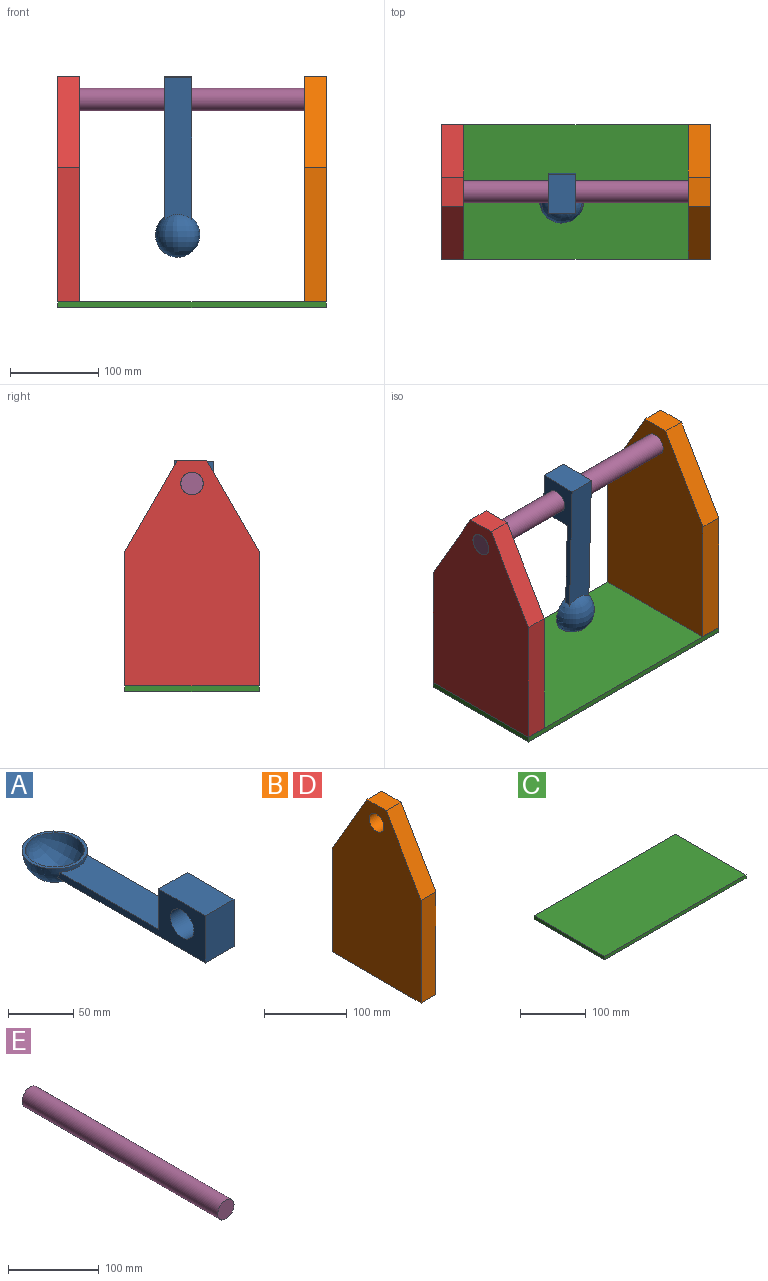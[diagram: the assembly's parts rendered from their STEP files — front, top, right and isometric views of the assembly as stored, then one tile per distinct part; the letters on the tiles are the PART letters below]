
ASSEMBLY  parts=5 mates=4
PART A: 11 faces, bbox 51.2x204.8x60.6 mm
  f0: plane 108.74x30.99mm, normal (0,0,1), area 3232.9mm2, adj f1,f4,f5,f8
  f1: revolved ~50.8x50.28mm, area 3765.8mm2, adj f0,f2,f4,f5,f6
  f2: plane 50.8x50.28mm, normal (0,0,1), area 382.5mm2, adj f1,f3
  f3: revolved ~45.72x45.2mm, area 3225.4mm2, adj f2
  f4: plane 162.81x45.22mm, normal (1,0,0), area 2429.9mm2, adj f0,f1,f6,f7,f8,f9,f10
  f5: plane 161.41x45.25mm, normal (-1,0,0), area 2421.6mm2, adj f0,f1,f6,f7,f8,f9,f10
  f6: plane 161.93x30.99mm, normal (0,0,-1), area 4866.7mm2, adj f1,f4,f5,f7
  f7: plane 44.34x30.98mm, normal (0,-1,0), area 1373.7mm2, adj f4,f5,f6,f9
  f8: plane 38.1x30.98mm, normal (0,1,0), area 1180.5mm2, adj f0,f4,f5,f9
  f9: plane 50.8x30.98mm, normal (0,0,1), area 1574mm2, adj f4,f5,f7,f8
  f10: cylinder r=12.7mm len=30.98mm, axis (1,0,0), area 2472.4mm2, adj f4,f5
PART B: 9 faces, bbox 25.4x152.4x255.6 mm
  f0: plane 152.4x25.4mm, normal (0,1,0), area 3871mm2, adj f1,f5,f7,f8
  f1: plane 103.2x59.58mm, normal (0,0.87,0.5), area 3026.8mm2, adj f0,f2,f7,f8
  f2: plane 33.24x25.4mm, normal (0,0,1), area 844.2mm2, adj f1,f3,f7,f8
  f3: plane 103.2x59.58mm, normal (0,-0.87,0.5), area 3026.8mm2, adj f2,f4,f7,f8
  f4: plane 152.4x25.4mm, normal (0,-1,0), area 3871mm2, adj f3,f5,f7,f8
  f5: plane 152.4x25.4mm, normal (0,0,-1), area 3871mm2, adj f0,f4,f7,f8
  f6: cylinder r=12.7mm len=25.4mm, axis (-1,0,0), area 2026.8mm2, adj f7,f8
  f7: plane 255.6x152.4mm, normal (1,0,0), area 32297.8mm2, adj f0,f1,f2,f3,f4,f5,f6
  f8: plane 255.6x152.4mm, normal (-1,0,0), area 32297.8mm2, adj f0,f1,f2,f3,f4,f5,f6
PART C: 6 faces, bbox 304.8x152.4x6.4 mm
  f0: plane 152.4x6.35mm, normal (1,0,0), area 967.7mm2, adj f1,f3,f4,f5
  f1: plane 304.8x6.35mm, normal (0,1,0), area 1935.5mm2, adj f0,f2,f4,f5
  f2: plane 152.4x6.35mm, normal (-1,0,0), area 967.7mm2, adj f1,f3,f4,f5
  f3: plane 304.8x6.35mm, normal (0,-1,0), area 1935.5mm2, adj f0,f2,f4,f5
  f4: plane 304.8x152.4mm, normal (0,0,1), area 46451.5mm2, adj f0,f1,f2,f3
  f5: plane 304.8x152.4mm, normal (0,0,-1), area 46451.5mm2, adj f0,f1,f2,f3
PART D: same geometry as B
PART E: 3 faces, bbox 25.4x304.8x25.4 mm
  f0: cylinder r=12.7mm len=304.8mm, axis (0,1,0), area 24322mm2, adj f1,f2
  f1: plane 25.4x25.4mm, normal (0,-1,0), area 506.7mm2, adj f0
  f2: plane 25.4x25.4mm, normal (0,1,0), area 506.7mm2, adj f0
PLACE A rot(axis=(-1,0,0),88.6deg) t=(-15.49,-10.33,83.06)mm
PLACE B t=(127,-76.2,6.35)mm
PLACE C at identity fixed
PLACE D t=(-152.4,-76.2,6.35)mm
PLACE E rot(axis=(0.71,0.71,0),180deg) t=(152.4,0,235.77)mm
MATE planar B.f5 <-> C.f4  axis (0,0,-1) through (152.4,76.2,6.35)mm
MATE pin_slot E.f0 <-> B.f6  axis (-1,0,0) through (-152.4,0,235.77)mm
MATE planar D.f5 <-> C.f4  axis (0,0,1) through (-152.4,76.2,6.35)mm
MATE pin_slot A.f10 <-> E.f0  axis (1,0,0) through (0,0,235.77)mm
